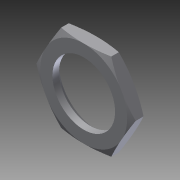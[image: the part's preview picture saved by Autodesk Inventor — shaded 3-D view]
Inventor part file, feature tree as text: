
AUTODESK INVENTOR PART (.ipt)
format: ipt  version: 2011 SP1 (Build 150282100, 282)  size: 119,808 bytes
history: native  units: in
note: dims shown in document units (in); Inventor stores cm internally (conversion verified against a paired STEP export)
features: other x7, sketch x3, revolve x1, extrude x1, hole x1
ambient origin geometry x8: Origin, YZ Plane, XZ Plane, XY Plane, X Axis, Y Axis, Z Axis, Center Point
bodies: Solid1 (feature_tree)
feature tree (13):
  revolve  "Revolution1"  [1 undecoded]
  extrude  "Extrusion1"  [1 undecoded]
  hole  "Drilling 1"  [1 undecoded]
  other  "nut_XY"
  other  "nut_YZ"
  other  "nut_ZX"
  other  "nut_X"
  other  "nut_Y"
  other  "nut_Z"
  other  "nut_Center"
  sketch  "Sketch_1"  dims[d0=360.0deg d1=0.158in d2=0.0in]
  sketch  "Sketch_2"  dims[d3=0.3979in d4=0.75in d5=0.472in d6=0.25in d7=0.6184in d8=0.079in d9=0.0in]
  sketch  "Sketch3"
note: 3 required parameter values undecoded (feature->parameter linkage not recoverable at this tier; creation-order binding heuristic only, values carry confidence <= 0.55)